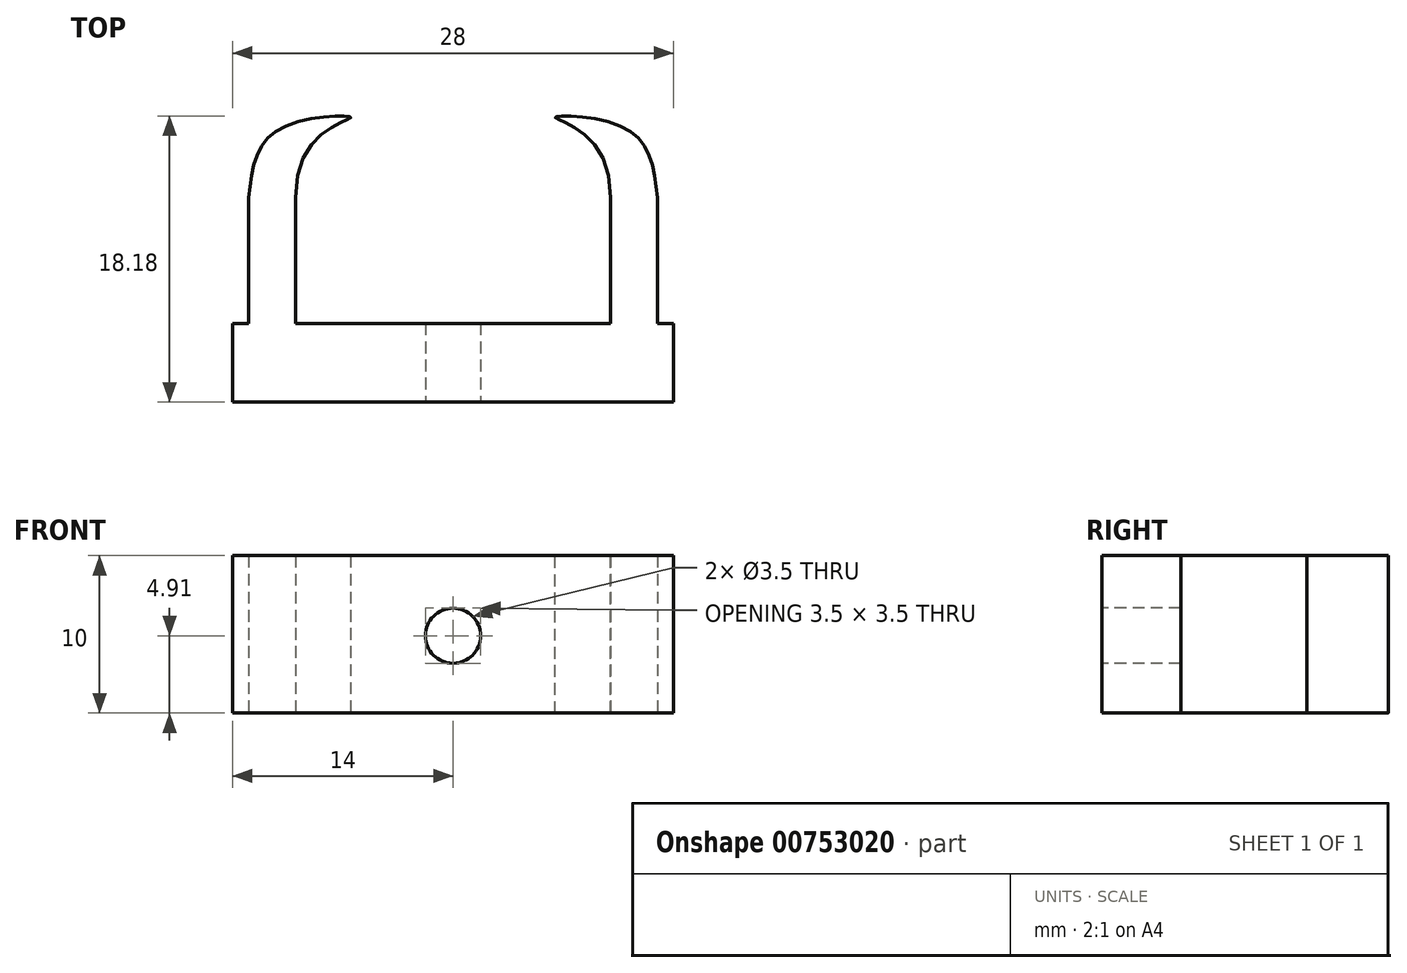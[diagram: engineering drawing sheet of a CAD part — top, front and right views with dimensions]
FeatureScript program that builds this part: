
annotation { "Feature Type Name" : "Feature", "Feature Type Description" : "" }
export const myFeature = defineFeature(function(context is Context, id is Id, definition is map)
    precondition{}
    {
        {
            var Q0;
            Q0=qCreatedBy(makeId("Top.planeOp"),FACE);
            var sketch = newSketch(context, id + "F0", { "sketchPlane" : qUnion([Q0])});
            skLineSegment(sketch, "E0", {"start": v(14, 0) * mm, "end": v(14, 5) * mm});
            skLineSegment(sketch, "E1", {"start": v(0, 49.97) * mm, "end": v(0, -44.66) * mm, "construction": true});
            skLineSegment(sketch, "E2", {"start": v(14, 0) * mm, "end": v(0, 0) * mm});
            skLineSegment(sketch, "E3.MirrorCS", {"start": v(-14, 0) * mm, "end": v(-14, 5) * mm});
            skLineSegment(sketch, "E4.MirrorCS", {"start": v(-14, 0) * mm, "end": v(0, 0) * mm});
            skLineSegment(sketch, "E5", {"start": v(-14, 5) * mm, "end": v(14, 5) * mm});
            skLineSegment(sketch, "E6", {"start": v(13, 5) * mm, "end": v(13, 13) * mm});
            skLineSegment(sketch, "E7", {"start": v(10, 5) * mm, "end": v(10, 13) * mm});
            skLineSegment(sketch, "E8.MirrorCS", {"start": v(-10, 5) * mm, "end": v(-10, 13) * mm});
            skLineSegment(sketch, "E9.MirrorCS", {"start": v(-13, 5) * mm, "end": v(-13, 13) * mm});
            skFitSpline(sketch, "E10", {"points": [v(10, 13) * mm, v(6.5, 18.1) * mm, v(11.06, 17.33) * mm, v(13, 13) * mm], "startDerivative": vector(0.72, 35.62) * mm, "endDerivative": vector(2.2, -16.14) * mm});
            skFitSpline(sketch, "E11.MirrorCS", {"points": [v(-10, 13) * mm, v(-6.5, 18.1) * mm, v(-11.06, 17.33) * mm, v(-13, 13) * mm], "startDerivative": vector(-0.72, 35.62) * mm, "endDerivative": vector(-2.2, -16.14) * mm});
            skSolve(sketch);
        }
        {
            var Q0;
            Q0 = qSketchRegion(id + "F0", true);
            extrude(context, id + "F1", {"entities" : qUnion([Q0]), "depth" : 10 * mm, "offsetDistance" : 25 * mm});
        }
        {
            var Q0;
            Q0=qCreatedBy(makeId("Front.planeOp"),FACE);
            var sketch = newSketch(context, id + "F2", { "sketchPlane" : qUnion([Q0])});
            skCircle(sketch, "E12", {"center": v(0, 4.9) * mm, "radius": 0.39 * mm});
            skSolve(sketch);
        }
        {
            var Q0;
            Q0=sQuery(id+"F2.wireOp",VERTEX,"E12.center");
            var Q1;
            Q1=makeQuery(id+"F1.opExtrude","SWEPT_BODY",BODY,{"disambiguationData":[OSD([sQuery(id+"F0.wireOp",EDGE,"E0"),sQuery(id+"F0.wireOp",EDGE,"E2"),sQuery(id+"F0.wireOp",EDGE,"E3.MirrorCS"),sQuery(id+"F0.wireOp",EDGE,"E4.MirrorCS"),sQuery(id+"F0.wireOp",EDGE,"E5"),sQuery(id+"F0.wireOp",EDGE,"E6"),sQuery(id+"F0.wireOp",EDGE,"E7"),sQuery(id+"F0.wireOp",EDGE,"E8.MirrorCS"),sQuery(id+"F0.wireOp",EDGE,"E9.MirrorCS"),sQuery(id+"F0.wireOp",EDGE,"E10"),sQuery(id+"F0.wireOp",EDGE,"E11.MirrorCS")])]});
            hole(context, id + "F3", {"style" : HoleStyle.SIMPLE, "endStyle" : HoleEndStyle.BLIND, "holeDiameter" : 3.5 * mm, "majorDiameter" : 5 * mm, "holeDepth" : 20 * mm, "isTappedThrough" : true, "tappedDepth" : 12 * mm, "tapClearance" : 3, "locations" : qUnion([Q0]), "scope" : qUnion([Q1])});
        }
    });
